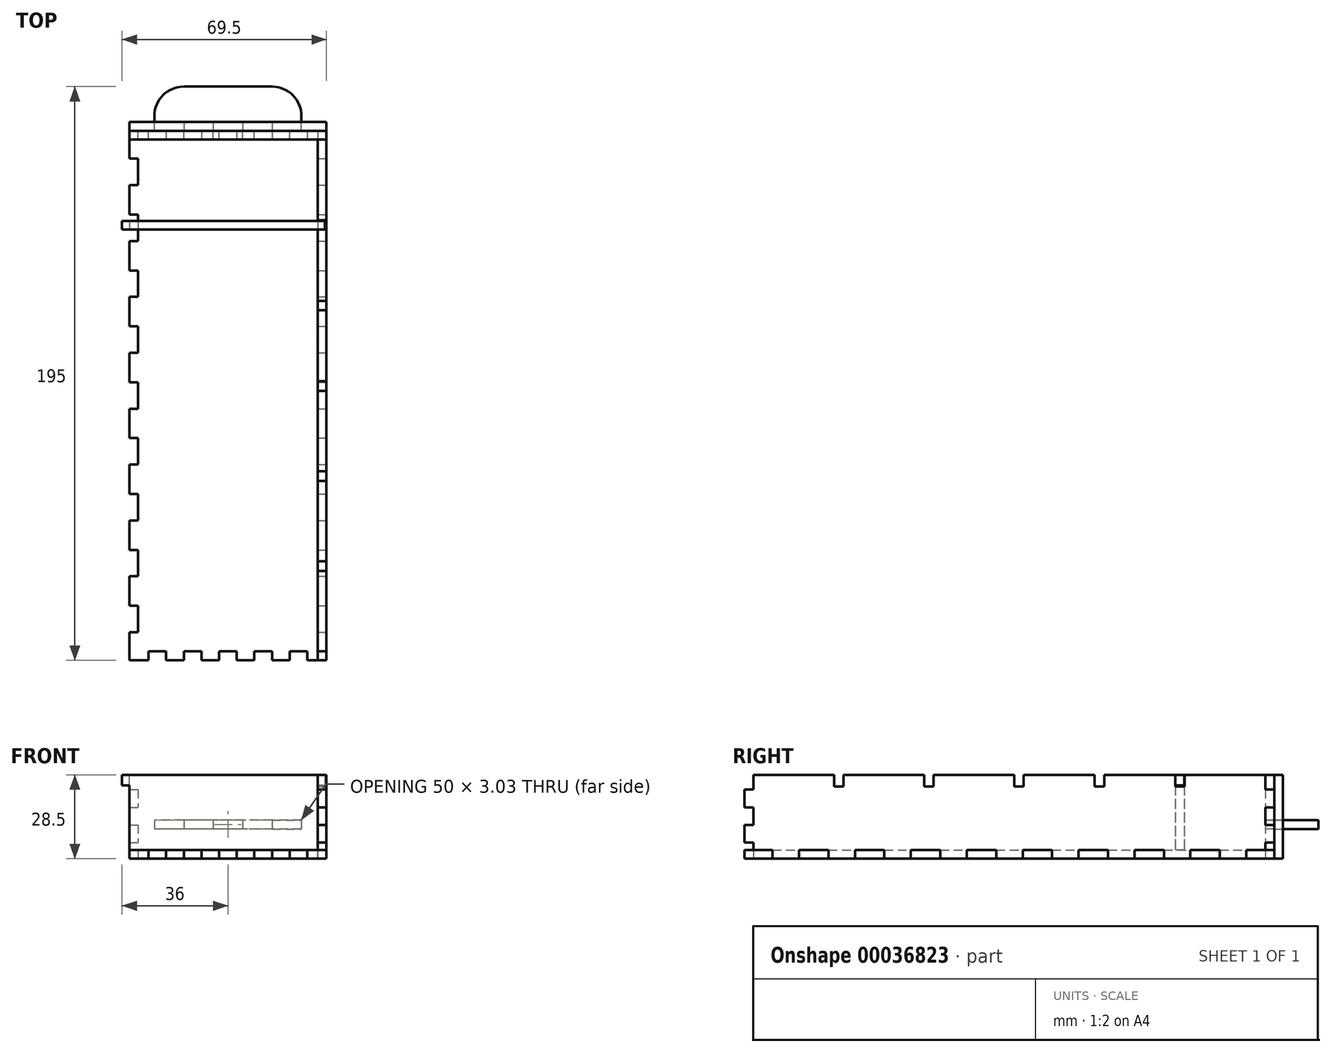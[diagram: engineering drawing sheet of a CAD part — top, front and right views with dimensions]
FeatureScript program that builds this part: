
annotation { "Feature Type Name" : "Feature", "Feature Type Description" : "" }
export const myFeature = defineFeature(function(context is Context, id is Id, definition is map)
    precondition{}
    {
        {
            var Q0;
            Q0=qCreatedBy(makeId("Front.planeOp"),FACE);
            var sketch = newSketch(context, id + "F0", { "sketchPlane" : qUnion([Q0])});
            skLineSegment(sketch, "E0.bottom", {"start": v(0, 0) * mm, "end": v(67, 0) * mm});
            skLineSegment(sketch, "E0.top", {"start": v(0, 28.5) * mm, "end": v(67, 28.5) * mm});
            skLineSegment(sketch, "E0.left", {"start": v(0, 0) * mm, "end": v(0, 28.5) * mm});
            skLineSegment(sketch, "E0.right", {"start": v(67, 0) * mm, "end": v(67, 28.5) * mm});
            skLineSegment(sketch, "E1.bottom", {"start": v(6.5, 0) * mm, "end": v(12.5, 0) * mm});
            skLineSegment(sketch, "E1.top", {"start": v(6.5, 3) * mm, "end": v(12.5, 3) * mm, "construction": true});
            skLineSegment(sketch, "E1.left", {"start": v(6.5, 0) * mm, "end": v(6.5, 3) * mm});
            skLineSegment(sketch, "E1.right", {"start": v(12.5, 0) * mm, "end": v(12.5, 3) * mm});
            skLineSegment(sketch, "E2.bottom", {"start": v(18.5, 0) * mm, "end": v(24.5, 0) * mm});
            skLineSegment(sketch, "E2.top", {"start": v(18.5, 3) * mm, "end": v(24.5, 3) * mm, "construction": true});
            skLineSegment(sketch, "E2.left", {"start": v(18.5, 0) * mm, "end": v(18.5, 3) * mm});
            skLineSegment(sketch, "E2.right", {"start": v(24.5, 0) * mm, "end": v(24.5, 3) * mm});
            skLineSegment(sketch, "E3.bottom", {"start": v(30.5, 0) * mm, "end": v(36.5, 0) * mm});
            skLineSegment(sketch, "E3.top", {"start": v(30.5, 3) * mm, "end": v(36.5, 3) * mm, "construction": true});
            skLineSegment(sketch, "E3.left", {"start": v(30.5, 0) * mm, "end": v(30.5, 3) * mm});
            skLineSegment(sketch, "E3.right", {"start": v(36.5, 0) * mm, "end": v(36.5, 3) * mm});
            skLineSegment(sketch, "E4.bottom", {"start": v(42.5, 0) * mm, "end": v(48.5, 0) * mm});
            skLineSegment(sketch, "E4.top", {"start": v(42.5, 3) * mm, "end": v(48.5, 3) * mm, "construction": true});
            skLineSegment(sketch, "E4.left", {"start": v(42.5, 0) * mm, "end": v(42.5, 3) * mm});
            skLineSegment(sketch, "E4.right", {"start": v(48.5, 0) * mm, "end": v(48.5, 3) * mm});
            skLineSegment(sketch, "E5.bottom", {"start": v(54.5, 0) * mm, "end": v(60.5, 0) * mm});
            skLineSegment(sketch, "E5.top", {"start": v(54.5, 3) * mm, "end": v(60.5, 3) * mm, "construction": true});
            skLineSegment(sketch, "E5.left", {"start": v(54.5, 0) * mm, "end": v(54.5, 3) * mm});
            skLineSegment(sketch, "E5.right", {"start": v(60.5, 0) * mm, "end": v(60.5, 3) * mm});
            skLineSegment(sketch, "E6.bottom", {"start": v(0, 23.5) * mm, "end": v(3, 23.5) * mm});
            skLineSegment(sketch, "E6.top", {"start": v(0, 17.5) * mm, "end": v(3, 17.5) * mm});
            skLineSegment(sketch, "E6.left", {"start": v(0, 23.5) * mm, "end": v(0, 17.5) * mm});
            skLineSegment(sketch, "E6.right", {"start": v(3, 23.5) * mm, "end": v(3, 17.5) * mm});
            skLineSegment(sketch, "E7.bottom", {"start": v(0, 11.5) * mm, "end": v(3, 11.5) * mm});
            skLineSegment(sketch, "E7.top", {"start": v(0, 5.5) * mm, "end": v(3, 5.5) * mm});
            skLineSegment(sketch, "E7.left", {"start": v(0, 11.5) * mm, "end": v(0, 5.5) * mm});
            skLineSegment(sketch, "E7.right", {"start": v(3, 11.5) * mm, "end": v(3, 5.5) * mm});
            skLineSegment(sketch, "E8.bottom", {"start": v(67, 23.5) * mm, "end": v(64, 23.5) * mm});
            skLineSegment(sketch, "E8.top", {"start": v(67, 17.5) * mm, "end": v(64, 17.5) * mm});
            skLineSegment(sketch, "E8.left", {"start": v(67, 23.5) * mm, "end": v(67, 17.5) * mm});
            skLineSegment(sketch, "E8.right", {"start": v(64, 23.5) * mm, "end": v(64, 17.5) * mm});
            skLineSegment(sketch, "E9.bottom", {"start": v(67, 11.5) * mm, "end": v(64, 11.5) * mm});
            skLineSegment(sketch, "E9.top", {"start": v(67, 5.5) * mm, "end": v(64, 5.5) * mm});
            skLineSegment(sketch, "E9.left", {"start": v(67, 11.5) * mm, "end": v(67, 5.5) * mm});
            skLineSegment(sketch, "E9.right", {"start": v(64, 11.5) * mm, "end": v(64, 5.5) * mm});
            skLineSegment(sketch, "E10", {"start": v(3, 17.5) * mm, "end": v(3, 11.5) * mm});
            skLineSegment(sketch, "E11", {"start": v(12.5, 3) * mm, "end": v(18.5, 3) * mm});
            skLineSegment(sketch, "E12", {"start": v(24.5, 3) * mm, "end": v(30.5, 3) * mm});
            skLineSegment(sketch, "E13", {"start": v(36.5, 3) * mm, "end": v(42.5, 3) * mm});
            skLineSegment(sketch, "E14", {"start": v(48.5, 3) * mm, "end": v(54.5, 3) * mm});
            skLineSegment(sketch, "E15", {"start": v(64, 11.5) * mm, "end": v(64, 17.5) * mm});
            skLineSegment(sketch, "E16", {"start": v(6.5, 3) * mm, "end": v(0, 3) * mm});
            skLineSegment(sketch, "E17", {"start": v(60.5, 3) * mm, "end": v(67, 3) * mm});
            skLineSegment(sketch, "E18.bottom", {"start": v(48.5, 13.14) * mm, "end": v(38.5, 13.14) * mm});
            skLineSegment(sketch, "E18.top", {"start": v(48.5, 10.1) * mm, "end": v(38.5, 10.1) * mm});
            skLineSegment(sketch, "E18.left", {"start": v(48.5, 13.14) * mm, "end": v(48.5, 10.1) * mm});
            skLineSegment(sketch, "E18.right", {"start": v(38.5, 13.14) * mm, "end": v(38.5, 10.1) * mm});
            skLineSegment(sketch, "E19.bottom", {"start": v(28.5, 13.14) * mm, "end": v(18.5, 13.14) * mm});
            skLineSegment(sketch, "E19.top", {"start": v(28.5, 10.1) * mm, "end": v(18.5, 10.1) * mm});
            skLineSegment(sketch, "E19.left", {"start": v(28.5, 13.14) * mm, "end": v(28.5, 10.1) * mm});
            skLineSegment(sketch, "E19.right", {"start": v(18.5, 13.14) * mm, "end": v(18.5, 10.1) * mm});
            skLineSegment(sketch, "E20.bottom", {"start": v(48.5, 10.1) * mm, "end": v(64, 10.1) * mm, "construction": true});
            skLineSegment(sketch, "E20.top", {"start": v(48.5, 10.1) * mm, "end": v(64, 10.1) * mm, "construction": true});
            skLineSegment(sketch, "E20.left", {"start": v(48.5, 10.1) * mm, "end": v(48.5, 10.1) * mm});
            skLineSegment(sketch, "E20.right", {"start": v(64, 10.1) * mm, "end": v(64, 10.1) * mm});
            skLineSegment(sketch, "E21.bottom", {"start": v(18.5, 10.1) * mm, "end": v(3, 10.1) * mm, "construction": true});
            skLineSegment(sketch, "E21.top", {"start": v(18.5, 10.1) * mm, "end": v(3, 10.1) * mm, "construction": true});
            skLineSegment(sketch, "E21.left", {"start": v(18.5, 10.1) * mm, "end": v(18.5, 10.1) * mm});
            skLineSegment(sketch, "E21.right", {"start": v(3, 10.1) * mm, "end": v(3, 10.1) * mm});
            skSolve(sketch);
        }
        {
            var Q0;
            {var subQ3=sQuery(id+"F0.wireOp",EDGE,"E0.top");Q0=makeQuery(id+"F0.imprint","IMPRINT",FACE,{"disambiguationData":[TD([[makeQuery(id+"F0.imprint","IMPRINT",EDGE,{"derivedFrom":subQ3}),-1.0]])]});}
            var Q1;
            {var subQ1=sQuery(id+"F0.wireOp",EDGE,"E6.top");Q1=makeQuery(id+"F0.imprint","IMPRINT",FACE,{"disambiguationData":[TD([[makeQuery(id+"F0.imprint","IMPRINT",EDGE,{"derivedFrom":subQ1}),-1.0]])]});}
            var Q2;
            {var subQ1=sQuery(id+"F0.wireOp",EDGE,"E8.top");Q2=makeQuery(id+"F0.imprint","IMPRINT",FACE,{"disambiguationData":[TD([[makeQuery(id+"F0.imprint","IMPRINT",EDGE,{"derivedFrom":subQ1}),1.0]])]});}
            extrude(context, id + "F1", {"entities" : qUnion([Q0, Q1, Q2]), "depth" : 3 * mm});
        }
        {
            var Q0;
            Q0=qCreatedBy(makeId("Top.planeOp"),FACE);
            var sketch = newSketch(context, id + "F2", { "sketchPlane" : qUnion([Q0])});
            skLineSegment(sketch, "E22.top", {"start": v(0, -180) * mm, "end": v(67, -180) * mm});
            skLineSegment(sketch, "E22.left", {"start": v(0, 0) * mm, "end": v(0, -180) * mm});
            skLineSegment(sketch, "E22.right", {"start": v(67, 0) * mm, "end": v(67, -180) * mm});
            skLineSegment(sketch, "E23.bottom", {"start": v(6.5, -180) * mm, "end": v(12.5, -180) * mm});
            skLineSegment(sketch, "E23.top", {"start": v(6.5, -177) * mm, "end": v(12.5, -177) * mm});
            skLineSegment(sketch, "E23.left", {"start": v(6.5, -180) * mm, "end": v(6.5, -177) * mm});
            skLineSegment(sketch, "E23.right", {"start": v(12.5, -180) * mm, "end": v(12.5, -177) * mm});
            skLineSegment(sketch, "E24.bottom", {"start": v(18.5, -180) * mm, "end": v(24.5, -180) * mm});
            skLineSegment(sketch, "E24.top", {"start": v(18.5, -177) * mm, "end": v(24.5, -177) * mm});
            skLineSegment(sketch, "E24.left", {"start": v(18.5, -180) * mm, "end": v(18.5, -177) * mm});
            skLineSegment(sketch, "E24.right", {"start": v(24.5, -180) * mm, "end": v(24.5, -177) * mm});
            skLineSegment(sketch, "E25.bottom", {"start": v(30.5, -180) * mm, "end": v(36.5, -180) * mm});
            skLineSegment(sketch, "E25.top", {"start": v(30.5, -177) * mm, "end": v(36.5, -177) * mm});
            skLineSegment(sketch, "E25.left", {"start": v(30.5, -180) * mm, "end": v(30.5, -177) * mm});
            skLineSegment(sketch, "E25.right", {"start": v(36.5, -180) * mm, "end": v(36.5, -177) * mm});
            skLineSegment(sketch, "E26.bottom", {"start": v(42.5, -180) * mm, "end": v(48.5, -180) * mm});
            skLineSegment(sketch, "E26.top", {"start": v(42.5, -177) * mm, "end": v(48.5, -177) * mm});
            skLineSegment(sketch, "E26.left", {"start": v(42.5, -180) * mm, "end": v(42.5, -177) * mm});
            skLineSegment(sketch, "E26.right", {"start": v(48.5, -180) * mm, "end": v(48.5, -177) * mm});
            skLineSegment(sketch, "E27.bottom", {"start": v(54.5, -180) * mm, "end": v(60.5, -180) * mm});
            skLineSegment(sketch, "E27.top", {"start": v(54.5, -177) * mm, "end": v(60.5, -177) * mm});
            skLineSegment(sketch, "E27.left", {"start": v(54.5, -180) * mm, "end": v(54.5, -177) * mm});
            skLineSegment(sketch, "E27.right", {"start": v(60.5, -180) * mm, "end": v(60.5, -177) * mm});
            skLineSegment(sketch, "E28.top", {"start": v(0, -18.5) * mm, "end": v(3, -18.5) * mm});
            skLineSegment(sketch, "E28.left", {"start": v(0, -9.5) * mm, "end": v(0, -18.5) * mm});
            skLineSegment(sketch, "E28.right", {"start": v(3, -9.5) * mm, "end": v(3, -18.5) * mm});
            skLineSegment(sketch, "E29.bottom", {"start": v(0, -28.5) * mm, "end": v(3, -28.5) * mm});
            skLineSegment(sketch, "E29.top", {"start": v(0, -37.5) * mm, "end": v(3, -37.5) * mm});
            skLineSegment(sketch, "E29.left", {"start": v(0, -28.5) * mm, "end": v(0, -37.5) * mm});
            skLineSegment(sketch, "E29.right", {"start": v(3, -28.5) * mm, "end": v(3, -37.5) * mm});
            skLineSegment(sketch, "E30.bottom", {"start": v(0, -47.5) * mm, "end": v(3, -47.5) * mm});
            skLineSegment(sketch, "E30.top", {"start": v(0, -56.5) * mm, "end": v(3, -56.5) * mm});
            skLineSegment(sketch, "E30.left", {"start": v(0, -47.5) * mm, "end": v(0, -56.5) * mm});
            skLineSegment(sketch, "E30.right", {"start": v(3, -47.5) * mm, "end": v(3, -56.5) * mm});
            skLineSegment(sketch, "E31.bottom", {"start": v(0, -66.5) * mm, "end": v(3, -66.5) * mm});
            skLineSegment(sketch, "E31.top", {"start": v(0, -75.5) * mm, "end": v(3, -75.5) * mm});
            skLineSegment(sketch, "E31.left", {"start": v(0, -66.5) * mm, "end": v(0, -75.5) * mm});
            skLineSegment(sketch, "E31.right", {"start": v(3, -66.5) * mm, "end": v(3, -75.5) * mm});
            skLineSegment(sketch, "E32.bottom", {"start": v(0, -85.5) * mm, "end": v(3, -85.5) * mm});
            skLineSegment(sketch, "E32.top", {"start": v(0, -94.5) * mm, "end": v(3, -94.5) * mm});
            skLineSegment(sketch, "E32.left", {"start": v(0, -85.5) * mm, "end": v(0, -94.5) * mm});
            skLineSegment(sketch, "E32.right", {"start": v(3, -85.5) * mm, "end": v(3, -94.5) * mm});
            skLineSegment(sketch, "E33.bottom", {"start": v(0, -104.5) * mm, "end": v(3, -104.5) * mm});
            skLineSegment(sketch, "E33.top", {"start": v(0, -113.5) * mm, "end": v(3, -113.5) * mm});
            skLineSegment(sketch, "E33.left", {"start": v(0, -104.5) * mm, "end": v(0, -113.5) * mm});
            skLineSegment(sketch, "E33.right", {"start": v(3, -104.5) * mm, "end": v(3, -113.5) * mm});
            skLineSegment(sketch, "E34.bottom", {"start": v(0, -123.5) * mm, "end": v(3, -123.5) * mm});
            skLineSegment(sketch, "E34.top", {"start": v(0, -132.5) * mm, "end": v(3, -132.5) * mm});
            skLineSegment(sketch, "E34.left", {"start": v(0, -123.5) * mm, "end": v(0, -132.5) * mm});
            skLineSegment(sketch, "E34.right", {"start": v(3, -123.5) * mm, "end": v(3, -132.5) * mm});
            skLineSegment(sketch, "E35.bottom", {"start": v(0, -142.5) * mm, "end": v(3, -142.5) * mm});
            skLineSegment(sketch, "E35.top", {"start": v(0, -151.5) * mm, "end": v(3, -151.5) * mm});
            skLineSegment(sketch, "E35.left", {"start": v(0, -142.5) * mm, "end": v(0, -151.5) * mm});
            skLineSegment(sketch, "E35.right", {"start": v(3, -142.5) * mm, "end": v(3, -151.5) * mm});
            skLineSegment(sketch, "E36.bottom", {"start": v(0, -161.5) * mm, "end": v(3, -161.5) * mm});
            skLineSegment(sketch, "E36.top", {"start": v(0, -170.5) * mm, "end": v(3, -170.5) * mm});
            skLineSegment(sketch, "E36.left", {"start": v(0, -161.5) * mm, "end": v(0, -170.5) * mm});
            skLineSegment(sketch, "E36.right", {"start": v(3, -161.5) * mm, "end": v(3, -170.5) * mm});
            skLineSegment(sketch, "E37", {"start": v(3, -161.5) * mm, "end": v(3, -151.5) * mm, "construction": true});
            skLineSegment(sketch, "E38", {"start": v(3, -142.5) * mm, "end": v(3, -132.5) * mm, "construction": true});
            skLineSegment(sketch, "E39", {"start": v(3, -123.5) * mm, "end": v(3, -113.5) * mm, "construction": true});
            skLineSegment(sketch, "E40", {"start": v(3, -104.5) * mm, "end": v(3, -94.5) * mm, "construction": true});
            skLineSegment(sketch, "E41", {"start": v(3, -18.5) * mm, "end": v(3, -28.5) * mm, "construction": true});
            skLineSegment(sketch, "E42", {"start": v(3, -37.5) * mm, "end": v(3, -47.5) * mm, "construction": true});
            skLineSegment(sketch, "E43", {"start": v(3, -56.5) * mm, "end": v(3, -66.5) * mm, "construction": true});
            skLineSegment(sketch, "E44", {"start": v(3, -75.5) * mm, "end": v(3, -85.5) * mm, "construction": true});
            skLineSegment(sketch, "E45", {"start": v(3, -170.5) * mm, "end": v(3, -177) * mm, "construction": true});
            skLineSegment(sketch, "E46.bottom", {"start": v(67, -170.5) * mm, "end": v(64, -170.5) * mm});
            skLineSegment(sketch, "E46.top", {"start": v(67, -161.5) * mm, "end": v(64, -161.5) * mm});
            skLineSegment(sketch, "E46.left", {"start": v(67, -170.5) * mm, "end": v(67, -161.5) * mm});
            skLineSegment(sketch, "E46.right", {"start": v(64, -170.5) * mm, "end": v(64, -161.5) * mm});
            skLineSegment(sketch, "E47.bottom", {"start": v(67, -151.5) * mm, "end": v(64, -151.5) * mm});
            skLineSegment(sketch, "E47.top", {"start": v(67, -142.5) * mm, "end": v(64, -142.5) * mm});
            skLineSegment(sketch, "E47.left", {"start": v(67, -151.5) * mm, "end": v(67, -142.5) * mm});
            skLineSegment(sketch, "E47.right", {"start": v(64, -151.5) * mm, "end": v(64, -142.5) * mm});
            skPoint(sketch, "E48.oppositeSnap0", {"position": v(1.5, -123.5) * mm});
            skLineSegment(sketch, "E48.bottom", {"start": v(67, -132.5) * mm, "end": v(64, -132.5) * mm});
            skLineSegment(sketch, "E48.top", {"start": v(67, -123.5) * mm, "end": v(64, -123.5) * mm});
            skLineSegment(sketch, "E48.left", {"start": v(67, -132.5) * mm, "end": v(67, -123.5) * mm});
            skLineSegment(sketch, "E48.right", {"start": v(64, -132.5) * mm, "end": v(64, -123.5) * mm});
            skPoint(sketch, "E49.firstSnap0", {"position": v(1.5, -113.5) * mm});
            skLineSegment(sketch, "E49.bottom", {"start": v(67, -113.5) * mm, "end": v(64, -113.5) * mm});
            skLineSegment(sketch, "E49.top", {"start": v(67, -104.5) * mm, "end": v(64, -104.5) * mm});
            skLineSegment(sketch, "E49.left", {"start": v(67, -113.5) * mm, "end": v(67, -104.5) * mm});
            skLineSegment(sketch, "E49.right", {"start": v(64, -113.5) * mm, "end": v(64, -104.5) * mm});
            skLineSegment(sketch, "E50.bottom", {"start": v(67, -94.5) * mm, "end": v(64, -94.5) * mm});
            skLineSegment(sketch, "E50.top", {"start": v(67, -85.5) * mm, "end": v(64, -85.5) * mm});
            skLineSegment(sketch, "E50.left", {"start": v(67, -94.5) * mm, "end": v(67, -85.5) * mm});
            skLineSegment(sketch, "E50.right", {"start": v(64, -94.5) * mm, "end": v(64, -85.5) * mm});
            skLineSegment(sketch, "E51.bottom", {"start": v(67, -75.5) * mm, "end": v(64, -75.5) * mm});
            skLineSegment(sketch, "E51.top", {"start": v(67, -66.5) * mm, "end": v(64, -66.5) * mm});
            skLineSegment(sketch, "E51.left", {"start": v(67, -75.5) * mm, "end": v(67, -66.5) * mm});
            skLineSegment(sketch, "E51.right", {"start": v(64, -75.5) * mm, "end": v(64, -66.5) * mm});
            skLineSegment(sketch, "E52.bottom", {"start": v(67, -56.5) * mm, "end": v(64, -56.5) * mm});
            skLineSegment(sketch, "E52.top", {"start": v(67, -47.5) * mm, "end": v(64, -47.5) * mm});
            skLineSegment(sketch, "E52.left", {"start": v(67, -56.5) * mm, "end": v(67, -47.5) * mm});
            skLineSegment(sketch, "E52.right", {"start": v(64, -56.5) * mm, "end": v(64, -47.5) * mm});
            skLineSegment(sketch, "E53.bottom", {"start": v(67, -37.5) * mm, "end": v(64, -37.5) * mm});
            skLineSegment(sketch, "E53.top", {"start": v(67, -28.5) * mm, "end": v(64, -28.5) * mm});
            skLineSegment(sketch, "E53.left", {"start": v(67, -37.5) * mm, "end": v(67, -28.5) * mm});
            skLineSegment(sketch, "E53.right", {"start": v(64, -37.5) * mm, "end": v(64, -28.5) * mm});
            skLineSegment(sketch, "E54.bottom", {"start": v(67, -18.5) * mm, "end": v(64, -18.5) * mm});
            skLineSegment(sketch, "E54.left", {"start": v(67, -18.5) * mm, "end": v(67, -9.5) * mm});
            skLineSegment(sketch, "E54.right", {"start": v(64, -18.5) * mm, "end": v(64, -9.5) * mm});
            skLineSegment(sketch, "E55.0.0", {"start": v(54.5, 0) * mm, "end": v(60.5, 0) * mm});
            skLineSegment(sketch, "E55.0.1", {"start": v(60.5, 0) * mm, "end": v(60.5, -3) * mm});
            skLineSegment(sketch, "E55.0.2", {"start": v(60.5, -3) * mm, "end": v(54.5, -3) * mm});
            skLineSegment(sketch, "E55.0.3", {"start": v(54.5, -3) * mm, "end": v(54.5, 0) * mm});
            skLineSegment(sketch, "E56.0.0", {"start": v(42.5, 0) * mm, "end": v(48.5, 0) * mm});
            skLineSegment(sketch, "E56.0.1", {"start": v(48.5, 0) * mm, "end": v(48.5, -3) * mm});
            skLineSegment(sketch, "E56.0.2", {"start": v(48.5, -3) * mm, "end": v(42.5, -3) * mm});
            skLineSegment(sketch, "E56.0.3", {"start": v(42.5, -3) * mm, "end": v(42.5, 0) * mm});
            skLineSegment(sketch, "E57.0.0", {"start": v(30.5, 0) * mm, "end": v(36.5, 0) * mm});
            skLineSegment(sketch, "E57.0.1", {"start": v(36.5, 0) * mm, "end": v(36.5, -3) * mm});
            skLineSegment(sketch, "E57.0.2", {"start": v(36.5, -3) * mm, "end": v(30.5, -3) * mm});
            skLineSegment(sketch, "E57.0.3", {"start": v(30.5, -3) * mm, "end": v(30.5, 0) * mm});
            skLineSegment(sketch, "E58.0.0", {"start": v(18.5, 0) * mm, "end": v(24.5, 0) * mm});
            skLineSegment(sketch, "E58.0.1", {"start": v(24.5, 0) * mm, "end": v(24.5, -3) * mm});
            skLineSegment(sketch, "E58.0.2", {"start": v(24.5, -3) * mm, "end": v(18.5, -3) * mm});
            skLineSegment(sketch, "E58.0.3", {"start": v(18.5, -3) * mm, "end": v(18.5, 0) * mm});
            skLineSegment(sketch, "E59.0.0", {"start": v(6.5, 0) * mm, "end": v(12.5, 0) * mm});
            skLineSegment(sketch, "E59.0.1", {"start": v(12.5, 0) * mm, "end": v(12.5, -3) * mm});
            skLineSegment(sketch, "E59.0.2", {"start": v(12.5, -3) * mm, "end": v(6.5, -3) * mm});
            skLineSegment(sketch, "E59.0.3", {"start": v(6.5, -3) * mm, "end": v(6.5, 0) * mm});
            skLineSegment(sketch, "E60", {"start": v(67, -9.5) * mm, "end": v(64, -9.5) * mm});
            skLineSegment(sketch, "E61", {"start": v(3, -9.5) * mm, "end": v(0, -9.5) * mm});
            skLineSegment(sketch, "E62", {"start": v(0, 0) * mm, "end": v(67, 0) * mm});
            skSolve(sketch);
        }
        {
            var Q0;
            Q0=makeQuery(id+"F2.imprint","IMPRINT",FACE,{"disambiguationData":[TD([[makeQuery(id+"F2.imprint","IMPRINT",EDGE,{"derivedFrom":sQuery(id+"F2.wireOp",EDGE,"E23.top")}),1.0]])]});
            extrude(context, id + "F3", {"entities" : qUnion([Q0]), "depth" : 3 * mm});
        }
        {
            var Q0;
            {var subQ0=sQuery(id+"F2.wireOp",EDGE,"E22.right");Q0=makeQuery(id+"F3.opExtrude","SWEPT_FACE",FACE,{"disambiguationData":[OSD([subQ0]),TDD([makeQuery(id+"F2.imprint","IMPRINT",EDGE,{"disambiguationData":[TD([[makeQuery(id+"F2.imprint","INTERSECT",VERTEX,{"derivedFrom":[subQ0,sQuery(id+"F2.wireOp",EDGE,"E53.top"),sQuery(id+"F2.wireOp",EDGE,"E53.left")]}),1.0]])],"derivedFrom":subQ0})])]});}
            var sketch = newSketch(context, id + "F4", { "sketchPlane" : qUnion([Q0])});
            skLineSegment(sketch, "E63.0.0", {"start": v(-18.5, 0) * mm, "end": v(-9.5, 0) * mm});
            skLineSegment(sketch, "E63.0.1", {"start": v(-9.5, 0) * mm, "end": v(-9.5, 3) * mm});
            skLineSegment(sketch, "E63.0.2", {"start": v(-9.5, 3) * mm, "end": v(-18.5, 3) * mm});
            skLineSegment(sketch, "E63.0.3", {"start": v(-18.5, 3) * mm, "end": v(-18.5, 0) * mm});
            skLineSegment(sketch, "E64.0.0", {"start": v(-37.5, 0) * mm, "end": v(-28.5, 0) * mm});
            skLineSegment(sketch, "E64.0.1", {"start": v(-28.5, 0) * mm, "end": v(-28.5, 3) * mm});
            skLineSegment(sketch, "E64.0.2", {"start": v(-28.5, 3) * mm, "end": v(-37.5, 3) * mm});
            skLineSegment(sketch, "E64.0.3", {"start": v(-37.5, 3) * mm, "end": v(-37.5, 0) * mm});
            skLineSegment(sketch, "E65.0.0", {"start": v(0, 5.5) * mm, "end": v(0, 11.5) * mm});
            skLineSegment(sketch, "E65.0.1", {"start": v(0, 11.5) * mm, "end": v(-3, 11.5) * mm});
            skLineSegment(sketch, "E65.0.2", {"start": v(-3, 11.5) * mm, "end": v(-3, 5.5) * mm});
            skLineSegment(sketch, "E65.0.3", {"start": v(-3, 5.5) * mm, "end": v(0, 5.5) * mm});
            skLineSegment(sketch, "E66.0.0", {"start": v(0, 17.5) * mm, "end": v(0, 23.5) * mm});
            skLineSegment(sketch, "E66.0.1", {"start": v(0, 23.5) * mm, "end": v(-3, 23.5) * mm});
            skLineSegment(sketch, "E66.0.2", {"start": v(-3, 23.5) * mm, "end": v(-3, 17.5) * mm});
            skLineSegment(sketch, "E66.0.3", {"start": v(-3, 17.5) * mm, "end": v(0, 17.5) * mm});
            skLineSegment(sketch, "E67.0.0", {"start": v(-56.5, 0) * mm, "end": v(-47.5, 0) * mm});
            skLineSegment(sketch, "E67.0.1", {"start": v(-47.5, 0) * mm, "end": v(-47.5, 3) * mm});
            skLineSegment(sketch, "E67.0.2", {"start": v(-47.5, 3) * mm, "end": v(-56.5, 3) * mm});
            skLineSegment(sketch, "E67.0.3", {"start": v(-56.5, 3) * mm, "end": v(-56.5, 0) * mm});
            skLineSegment(sketch, "E68.0.0", {"start": v(-75.5, 0) * mm, "end": v(-66.5, 0) * mm});
            skLineSegment(sketch, "E68.0.1", {"start": v(-66.5, 0) * mm, "end": v(-66.5, 3) * mm});
            skLineSegment(sketch, "E68.0.2", {"start": v(-66.5, 3) * mm, "end": v(-75.5, 3) * mm});
            skLineSegment(sketch, "E68.0.3", {"start": v(-75.5, 3) * mm, "end": v(-75.5, 0) * mm});
            skLineSegment(sketch, "E69.0.0", {"start": v(-94.5, 0) * mm, "end": v(-85.5, 0) * mm});
            skLineSegment(sketch, "E69.0.1", {"start": v(-85.5, 0) * mm, "end": v(-85.5, 3) * mm});
            skLineSegment(sketch, "E69.0.2", {"start": v(-85.5, 3) * mm, "end": v(-94.5, 3) * mm});
            skLineSegment(sketch, "E69.0.3", {"start": v(-94.5, 3) * mm, "end": v(-94.5, 0) * mm});
            skLineSegment(sketch, "E70.0.0", {"start": v(-113.5, 0) * mm, "end": v(-104.5, 0) * mm});
            skLineSegment(sketch, "E70.0.1", {"start": v(-104.5, 0) * mm, "end": v(-104.5, 3) * mm});
            skLineSegment(sketch, "E70.0.2", {"start": v(-104.5, 3) * mm, "end": v(-113.5, 3) * mm});
            skLineSegment(sketch, "E70.0.3", {"start": v(-113.5, 3) * mm, "end": v(-113.5, 0) * mm});
            skLineSegment(sketch, "E71.0.0", {"start": v(-132.5, 0) * mm, "end": v(-123.5, 0) * mm});
            skLineSegment(sketch, "E71.0.1", {"start": v(-123.5, 0) * mm, "end": v(-123.5, 3) * mm});
            skLineSegment(sketch, "E71.0.2", {"start": v(-123.5, 3) * mm, "end": v(-132.5, 3) * mm});
            skLineSegment(sketch, "E71.0.3", {"start": v(-132.5, 3) * mm, "end": v(-132.5, 0) * mm});
            skLineSegment(sketch, "E72.0.0", {"start": v(-170.5, 0) * mm, "end": v(-161.5, 0) * mm});
            skLineSegment(sketch, "E72.0.1", {"start": v(-161.5, 0) * mm, "end": v(-161.5, 3) * mm});
            skLineSegment(sketch, "E72.0.2", {"start": v(-161.5, 3) * mm, "end": v(-170.5, 3) * mm});
            skLineSegment(sketch, "E72.0.3", {"start": v(-170.5, 3) * mm, "end": v(-170.5, 0) * mm});
            skLineSegment(sketch, "E73.0.0", {"start": v(-151.5, 0) * mm, "end": v(-142.5, 0) * mm});
            skLineSegment(sketch, "E73.0.1", {"start": v(-142.5, 0) * mm, "end": v(-142.5, 3) * mm});
            skLineSegment(sketch, "E73.0.2", {"start": v(-142.5, 3) * mm, "end": v(-151.5, 3) * mm});
            skLineSegment(sketch, "E73.0.3", {"start": v(-151.5, 3) * mm, "end": v(-151.5, 0) * mm});
            skLineSegment(sketch, "E74.bottom", {"start": v(-180, 23.5) * mm, "end": v(-177, 23.5) * mm});
            skLineSegment(sketch, "E74.top", {"start": v(-180, 17.5) * mm, "end": v(-177, 17.5) * mm});
            skLineSegment(sketch, "E74.left", {"start": v(-180, 23.5) * mm, "end": v(-180, 17.5) * mm});
            skLineSegment(sketch, "E74.right", {"start": v(-177, 23.5) * mm, "end": v(-177, 17.5) * mm});
            skLineSegment(sketch, "E75.bottom", {"start": v(-180, 11.5) * mm, "end": v(-177, 11.5) * mm});
            skLineSegment(sketch, "E75.top", {"start": v(-180, 5.5) * mm, "end": v(-177, 5.5) * mm});
            skLineSegment(sketch, "E75.left", {"start": v(-180, 11.5) * mm, "end": v(-180, 5.5) * mm});
            skLineSegment(sketch, "E75.right", {"start": v(-177, 11.5) * mm, "end": v(-177, 5.5) * mm});
            skLineSegment(sketch, "E76.bottom", {"start": v(0, 0.09) * mm, "end": v(-180, 0.09) * mm});
            skLineSegment(sketch, "E76.top", {"start": v(0, 28.5) * mm, "end": v(-180, 28.5) * mm});
            skLineSegment(sketch, "E76.left", {"start": v(0, 0.09) * mm, "end": v(0, 28.5) * mm});
            skLineSegment(sketch, "E76.right", {"start": v(-180, 0.09) * mm, "end": v(-180, 28.5) * mm});
            skLineSegment(sketch, "E77.0.0", {"start": v(-85.5, 0) * mm, "end": v(-75.5, 0) * mm});
            skLineSegment(sketch, "E77.0.1", {"start": v(-75.5, 0) * mm, "end": v(-75.5, 3) * mm});
            skLineSegment(sketch, "E77.0.2", {"start": v(-75.5, 3) * mm, "end": v(-85.5, 3) * mm});
            skLineSegment(sketch, "E77.0.3", {"start": v(-85.5, 3) * mm, "end": v(-85.5, 0) * mm});
            skLineSegment(sketch, "E78.0.0", {"start": v(-66.5, 0) * mm, "end": v(-56.5, 0) * mm});
            skLineSegment(sketch, "E78.0.1", {"start": v(-56.5, 0) * mm, "end": v(-56.5, 3) * mm});
            skLineSegment(sketch, "E78.0.2", {"start": v(-56.5, 3) * mm, "end": v(-66.5, 3) * mm});
            skLineSegment(sketch, "E78.0.3", {"start": v(-66.5, 3) * mm, "end": v(-66.5, 0) * mm});
            skLineSegment(sketch, "E79.0.0", {"start": v(-47.5, 0) * mm, "end": v(-37.5, 0) * mm});
            skLineSegment(sketch, "E79.0.1", {"start": v(-37.5, 0) * mm, "end": v(-37.5, 3) * mm});
            skLineSegment(sketch, "E79.0.2", {"start": v(-37.5, 3) * mm, "end": v(-47.5, 3) * mm});
            skLineSegment(sketch, "E79.0.3", {"start": v(-47.5, 3) * mm, "end": v(-47.5, 0) * mm});
            skLineSegment(sketch, "E80.0.0", {"start": v(-28.5, 0) * mm, "end": v(-18.5, 0) * mm});
            skLineSegment(sketch, "E80.0.1", {"start": v(-18.5, 0) * mm, "end": v(-18.5, 3) * mm});
            skLineSegment(sketch, "E80.0.2", {"start": v(-18.5, 3) * mm, "end": v(-28.5, 3) * mm});
            skLineSegment(sketch, "E80.0.3", {"start": v(-28.5, 3) * mm, "end": v(-28.5, 0) * mm});
            skLineSegment(sketch, "E81.0.0", {"start": v(-9.5, 0) * mm, "end": v(0, 0) * mm});
            skLineSegment(sketch, "E81.0.1", {"start": v(0, 0) * mm, "end": v(0, 3) * mm});
            skLineSegment(sketch, "E81.0.2", {"start": v(0, 3) * mm, "end": v(-9.5, 3) * mm});
            skLineSegment(sketch, "E81.0.3", {"start": v(-9.5, 3) * mm, "end": v(-9.5, 0) * mm});
            skLineSegment(sketch, "E82.0.0", {"start": v(0, 11.5) * mm, "end": v(0, 17.5) * mm});
            skLineSegment(sketch, "E82.0.1", {"start": v(0, 17.5) * mm, "end": v(-3, 17.5) * mm});
            skLineSegment(sketch, "E82.0.2", {"start": v(-3, 17.5) * mm, "end": v(-3, 11.5) * mm});
            skLineSegment(sketch, "E82.0.3", {"start": v(-3, 11.5) * mm, "end": v(0, 11.5) * mm});
            skLineSegment(sketch, "E83.0.0", {"start": v(0, 23.5) * mm, "end": v(0, 28.5) * mm});
            skLineSegment(sketch, "E83.0.1", {"start": v(0, 28.5) * mm, "end": v(-3, 28.5) * mm});
            skLineSegment(sketch, "E83.0.2", {"start": v(-3, 28.5) * mm, "end": v(-3, 23.5) * mm});
            skLineSegment(sketch, "E83.0.3", {"start": v(-3, 23.5) * mm, "end": v(0, 23.5) * mm});
            skLineSegment(sketch, "E84.0.0", {"start": v(0, 3) * mm, "end": v(0, 5.5) * mm});
            skLineSegment(sketch, "E84.0.1", {"start": v(0, 5.5) * mm, "end": v(-3, 5.5) * mm});
            skLineSegment(sketch, "E84.0.2", {"start": v(-3, 5.5) * mm, "end": v(-3, 3) * mm});
            skLineSegment(sketch, "E84.0.3", {"start": v(-3, 3) * mm, "end": v(0, 3) * mm});
            skLineSegment(sketch, "E85.0.0", {"start": v(-104.5, 0) * mm, "end": v(-94.5, 0) * mm});
            skLineSegment(sketch, "E85.0.1", {"start": v(-94.5, 0) * mm, "end": v(-94.5, 3) * mm});
            skLineSegment(sketch, "E85.0.2", {"start": v(-94.5, 3) * mm, "end": v(-104.5, 3) * mm});
            skLineSegment(sketch, "E85.0.3", {"start": v(-104.5, 3) * mm, "end": v(-104.5, 0) * mm});
            skLineSegment(sketch, "E86.0.0", {"start": v(-123.5, 0) * mm, "end": v(-113.5, 0) * mm});
            skLineSegment(sketch, "E86.0.1", {"start": v(-113.5, 0) * mm, "end": v(-113.5, 3) * mm});
            skLineSegment(sketch, "E86.0.2", {"start": v(-113.5, 3) * mm, "end": v(-123.5, 3) * mm});
            skLineSegment(sketch, "E86.0.3", {"start": v(-123.5, 3) * mm, "end": v(-123.5, 0) * mm});
            skLineSegment(sketch, "E87.0.0", {"start": v(-142.5, 0) * mm, "end": v(-132.5, 0) * mm});
            skLineSegment(sketch, "E87.0.1", {"start": v(-132.5, 0) * mm, "end": v(-132.5, 3) * mm});
            skLineSegment(sketch, "E87.0.2", {"start": v(-132.5, 3) * mm, "end": v(-142.5, 3) * mm});
            skLineSegment(sketch, "E87.0.3", {"start": v(-142.5, 3) * mm, "end": v(-142.5, 0) * mm});
            skLineSegment(sketch, "E88.0.0", {"start": v(-161.5, 0) * mm, "end": v(-151.5, 0) * mm});
            skLineSegment(sketch, "E88.0.1", {"start": v(-151.5, 0) * mm, "end": v(-151.5, 3) * mm});
            skLineSegment(sketch, "E88.0.2", {"start": v(-151.5, 3) * mm, "end": v(-161.5, 3) * mm});
            skLineSegment(sketch, "E88.0.3", {"start": v(-161.5, 3) * mm, "end": v(-161.5, 0) * mm});
            skLineSegment(sketch, "E89.0.0", {"start": v(-180, 0) * mm, "end": v(-170.5, 0) * mm});
            skLineSegment(sketch, "E89.0.1", {"start": v(-170.5, 0) * mm, "end": v(-170.5, 3) * mm});
            skLineSegment(sketch, "E89.0.2", {"start": v(-170.5, 3) * mm, "end": v(-180, 3) * mm});
            skLineSegment(sketch, "E89.0.3", {"start": v(-180, 3) * mm, "end": v(-180, 0) * mm});
            skLineSegment(sketch, "E90", {"start": v(-177, 5.5) * mm, "end": v(-177, 3) * mm});
            skLineSegment(sketch, "E91", {"start": v(-177, 23.5) * mm, "end": v(-177, 28.5) * mm});
            skLineSegment(sketch, "E92", {"start": v(-177, 17.5) * mm, "end": v(-177, 11.5) * mm});
            skSolve(sketch);
        }
        {
            var Q0;
            Q0=makeQuery(id+"F4.imprint","IMPRINT",FACE,{"disambiguationData":[TD([[makeQuery(id+"F4.imprint","IMPRINT",EDGE,{"derivedFrom":sQuery(id+"F4.wireOp",EDGE,"E63.0.2")}),-1.0]])]});
            var Q1;
            {var subQ3=sQuery(id+"F4.wireOp",EDGE,"E72.0.2");Q1=makeQuery(id+"F4.imprint","IMPRINT",FACE,{"disambiguationData":[TD([[makeQuery(id+"F4.imprint","IMPRINT",EDGE,{"derivedFrom":subQ3}),1.0]])]});}
            var Q2;
            {var subQ3=sQuery(id+"F4.wireOp",EDGE,"E73.0.2");Q2=makeQuery(id+"F4.imprint","IMPRINT",FACE,{"disambiguationData":[TD([[makeQuery(id+"F4.imprint","IMPRINT",EDGE,{"derivedFrom":subQ3}),1.0]])]});}
            var Q3;
            {var subQ3=sQuery(id+"F4.wireOp",EDGE,"E71.0.2");Q3=makeQuery(id+"F4.imprint","IMPRINT",FACE,{"disambiguationData":[TD([[makeQuery(id+"F4.imprint","IMPRINT",EDGE,{"derivedFrom":subQ3}),1.0]])]});}
            var Q4;
            {var subQ3=sQuery(id+"F4.wireOp",EDGE,"E70.0.2");Q4=makeQuery(id+"F4.imprint","IMPRINT",FACE,{"disambiguationData":[TD([[makeQuery(id+"F4.imprint","IMPRINT",EDGE,{"derivedFrom":subQ3}),1.0]])]});}
            var Q5;
            {var subQ3=sQuery(id+"F4.wireOp",EDGE,"E69.0.2");Q5=makeQuery(id+"F4.imprint","IMPRINT",FACE,{"disambiguationData":[TD([[makeQuery(id+"F4.imprint","IMPRINT",EDGE,{"derivedFrom":subQ3}),1.0]])]});}
            var Q6;
            {var subQ3=sQuery(id+"F4.wireOp",EDGE,"E68.0.2");Q6=makeQuery(id+"F4.imprint","IMPRINT",FACE,{"disambiguationData":[TD([[makeQuery(id+"F4.imprint","IMPRINT",EDGE,{"derivedFrom":subQ3}),1.0]])]});}
            var Q7;
            {var subQ3=sQuery(id+"F4.wireOp",EDGE,"E67.0.2");Q7=makeQuery(id+"F4.imprint","IMPRINT",FACE,{"disambiguationData":[TD([[makeQuery(id+"F4.imprint","IMPRINT",EDGE,{"derivedFrom":subQ3}),1.0]])]});}
            var Q8;
            {var subQ3=sQuery(id+"F4.wireOp",EDGE,"E64.0.2");Q8=makeQuery(id+"F4.imprint","IMPRINT",FACE,{"disambiguationData":[TD([[makeQuery(id+"F4.imprint","IMPRINT",EDGE,{"derivedFrom":subQ3}),1.0]])]});}
            var Q9;
            {var subQ3=sQuery(id+"F4.wireOp",EDGE,"E63.0.2");Q9=makeQuery(id+"F4.imprint","IMPRINT",FACE,{"disambiguationData":[TD([[makeQuery(id+"F4.imprint","IMPRINT",EDGE,{"derivedFrom":subQ3}),1.0]])]});}
            var Q10;
            Q10=makeQuery(id+"F4.imprint","IMPRINT",FACE,{"disambiguationData":[TD([[makeQuery(id+"F4.imprint","IMPRINT",EDGE,{"derivedFrom":sQuery(id+"F4.wireOp",EDGE,"E65.0.2")}),1.0]])]});
            var Q11;
            Q11=makeQuery(id+"F4.imprint","IMPRINT",FACE,{"disambiguationData":[TD([[makeQuery(id+"F4.imprint","IMPRINT",EDGE,{"derivedFrom":sQuery(id+"F4.wireOp",EDGE,"E66.0.2")}),1.0]])]});
            var Q12;
            {var subQ2=sQuery(id+"F4.wireOp",EDGE,"E75.bottom");Q12=makeQuery(id+"F4.imprint","IMPRINT",FACE,{"disambiguationData":[TD([[makeQuery(id+"F4.imprint","IMPRINT",EDGE,{"derivedFrom":subQ2}),-1.0]])]});}
            var Q13;
            {var subQ2=sQuery(id+"F4.wireOp",EDGE,"E74.bottom");Q13=makeQuery(id+"F4.imprint","IMPRINT",FACE,{"disambiguationData":[TD([[makeQuery(id+"F4.imprint","IMPRINT",EDGE,{"derivedFrom":subQ2}),-1.0]])]});}
            extrude(context, id + "F5", {"entities" : qUnion([Q0, Q1, Q2, Q3, Q4, Q5, Q6, Q7, Q8, Q9, Q10, Q11, Q12, Q13]), "oppositeDirection" : true, "depth" : 3 * mm});
        }
        {
            var Q0;
            Q0=makeQuery(id+"F1.opExtrude","SWEPT_FACE",FACE,{"disambiguationData":[OSD([sQuery(id+"F0.wireOp",EDGE,"E18.top")])]});
            var sketch = newSketch(context, id + "F6", { "sketchPlane" : qUnion([Q0])});
            skLineSegment(sketch, "E93.bottom", {"start": v(58.5, -3) * mm, "end": v(8.5, -3) * mm});
            skLineSegment(sketch, "E93.top", {"start": v(48.5, 15) * mm, "end": v(18.5, 15) * mm});
            skLineSegment(sketch, "E93.left", {"start": v(58.5, -3) * mm, "end": v(58.5, 5) * mm});
            skLineSegment(sketch, "E93.right", {"start": v(8.5, -3) * mm, "end": v(8.5, 5) * mm});
            skLineSegment(sketch, "E94", {"start": v(58.5, -3) * mm, "end": v(48.5, -3) * mm, "construction": true});
            skLineSegment(sketch, "E95", {"start": v(48.5, -3) * mm, "end": v(58.5, -3) * mm, "construction": true});
            skLineSegment(sketch, "E96.0.0", {"start": v(28.5, 0) * mm, "end": v(18.5, 0) * mm, "construction": true});
            skLineSegment(sketch, "E96.0.1", {"start": v(18.5, 0) * mm, "end": v(18.5, -3) * mm, "construction": true});
            skLineSegment(sketch, "E96.0.2", {"start": v(18.5, -3) * mm, "end": v(28.5, -3) * mm, "construction": true});
            skLineSegment(sketch, "E96.0.3", {"start": v(28.5, -3) * mm, "end": v(28.5, 0) * mm, "construction": true});
            skLineSegment(sketch, "E97.0.0", {"start": v(48.5, 0) * mm, "end": v(38.5, 0) * mm, "construction": true});
            skLineSegment(sketch, "E97.0.1", {"start": v(38.5, 0) * mm, "end": v(38.5, -3) * mm, "construction": true});
            skLineSegment(sketch, "E97.0.2", {"start": v(38.5, -3) * mm, "end": v(48.5, -3) * mm, "construction": true});
            skLineSegment(sketch, "E97.0.3", {"start": v(48.5, -3) * mm, "end": v(48.5, 0) * mm, "construction": true});
            skLineSegment(sketch, "E98", {"start": v(8.5, -3) * mm, "end": v(18.5, -3) * mm, "construction": true});
            skPoint(sketch, "E99.visualSharp", {"position": v(8.5, 15) * mm});
            skArc(sketch, "E99.filletArc", {"start": v(18.5, 15) * mm, "mid": v(11.43, 12.07) * mm, "end": v(8.5, 5) * mm});
            skPoint(sketch, "E100.visualSharp", {"position": v(58.5, 15) * mm});
            skArc(sketch, "E100.filletArc", {"start": v(58.5, 5) * mm, "mid": v(55.57, 12.07) * mm, "end": v(48.5, 15) * mm});
            skLineSegment(sketch, "E101.0.0", {"start": v(28.5, 0) * mm, "end": v(18.5, 0) * mm});
            skLineSegment(sketch, "E101.0.1", {"start": v(18.5, 0) * mm, "end": v(18.5, -3) * mm});
            skLineSegment(sketch, "E101.0.2", {"start": v(18.5, -3) * mm, "end": v(28.5, -3) * mm});
            skLineSegment(sketch, "E101.0.3", {"start": v(28.5, -3) * mm, "end": v(28.5, 0) * mm});
            skLineSegment(sketch, "E102", {"start": v(48.5, 0) * mm, "end": v(58.5, 0) * mm});
            skLineSegment(sketch, "E103", {"start": v(38.5, 0) * mm, "end": v(28.5, 0) * mm});
            skLineSegment(sketch, "E104", {"start": v(18.5, 0) * mm, "end": v(8.5, 0) * mm});
            skSolve(sketch);
        }
        {
            var Q0;
            Q0=makeQuery(id+"F6.imprint","IMPRINT",FACE,{"disambiguationData":[TD([[makeQuery(id+"F6.imprint","IMPRINT",EDGE,{"derivedFrom":sQuery(id+"F6.wireOp",EDGE,"E93.top")}),1.0]])]});
            var Q1;
            Q1=makeQuery(id+"F6.imprint","IMPRINT",FACE,{"disambiguationData":[TD([[makeQuery(id+"F6.imprint","IMPRINT",EDGE,{"derivedFrom":sQuery(id+"F6.wireOp",EDGE,"E101.0.0")}),1.0]])]});
            var Q2;
            {var subQ0=sQuery(id+"F0.wireOp",EDGE,"E18.top");Q2=makeQuery(id+"F6.imprint","IMPRINT",FACE,{"disambiguationData":[TD([[makeQuery(id+"F6.imprint","IMPRINT",EDGE,{"derivedFrom":makeQuery(id+"F1.opExtrude","CAP_EDGE",EDGE,{"disambiguationData":[OSD([subQ0])],"isStart":true})}),1.0]])]});}
            extrude(context, id + "F7", {"entities" : qUnion([Q0, Q1, Q2]), "depth" : 3 * mm});
        }
        {
            var Q0;
            Q0=makeQuery(id+"F1.opExtrude","CAP_FACE",FACE,{"disambiguationData":[OSD([sQuery(id+"F0.wireOp",EDGE,"E0.top"),sQuery(id+"F0.wireOp",EDGE,"E0.left"),sQuery(id+"F0.wireOp",EDGE,"E0.right"),sQuery(id+"F0.wireOp",EDGE,"E1.bottom"),sQuery(id+"F0.wireOp",EDGE,"E1.left"),sQuery(id+"F0.wireOp",EDGE,"E1.right"),sQuery(id+"F0.wireOp",EDGE,"E2.bottom"),sQuery(id+"F0.wireOp",EDGE,"E2.left"),sQuery(id+"F0.wireOp",EDGE,"E2.right"),sQuery(id+"F0.wireOp",EDGE,"E3.bottom"),sQuery(id+"F0.wireOp",EDGE,"E3.left"),sQuery(id+"F0.wireOp",EDGE,"E3.right"),sQuery(id+"F0.wireOp",EDGE,"E4.bottom"),sQuery(id+"F0.wireOp",EDGE,"E4.left"),sQuery(id+"F0.wireOp",EDGE,"E4.right"),sQuery(id+"F0.wireOp",EDGE,"E5.bottom"),sQuery(id+"F0.wireOp",EDGE,"E5.left"),sQuery(id+"F0.wireOp",EDGE,"E5.right"),sQuery(id+"F0.wireOp",EDGE,"E6.bottom"),sQuery(id+"F0.wireOp",EDGE,"E6.top"),sQuery(id+"F0.wireOp",EDGE,"E6.right"),sQuery(id+"F0.wireOp",EDGE,"E7.bottom"),sQuery(id+"F0.wireOp",EDGE,"E7.top"),sQuery(id+"F0.wireOp",EDGE,"E7.right"),sQuery(id+"F0.wireOp",EDGE,"E8.bottom"),sQuery(id+"F0.wireOp",EDGE,"E8.top"),sQuery(id+"F0.wireOp",EDGE,"E8.right"),sQuery(id+"F0.wireOp",EDGE,"E9.bottom"),sQuery(id+"F0.wireOp",EDGE,"E9.top"),sQuery(id+"F0.wireOp",EDGE,"E9.right"),sQuery(id+"F0.wireOp",EDGE,"E11"),sQuery(id+"F0.wireOp",EDGE,"E12"),sQuery(id+"F0.wireOp",EDGE,"E13"),sQuery(id+"F0.wireOp",EDGE,"E14"),sQuery(id+"F0.wireOp",EDGE,"E16"),sQuery(id+"F0.wireOp",EDGE,"E17"),sQuery(id+"F0.wireOp",EDGE,"E18.bottom"),sQuery(id+"F0.wireOp",EDGE,"E18.top"),sQuery(id+"F0.wireOp",EDGE,"E18.left"),sQuery(id+"F0.wireOp",EDGE,"E18.right"),sQuery(id+"F0.wireOp",EDGE,"E19.bottom"),sQuery(id+"F0.wireOp",EDGE,"E19.top"),sQuery(id+"F0.wireOp",EDGE,"E19.left"),sQuery(id+"F0.wireOp",EDGE,"E19.right")])],"isStart":true});
            var sketch = newSketch(context, id + "F8", { "sketchPlane" : qUnion([Q0])});
            skLineSegment(sketch, "E105.0.0", {"start": v(0, 28.5) * mm, "end": v(-67, 28.5) * mm});
            skLineSegment(sketch, "E105.0.1", {"start": v(-67, 28.5) * mm, "end": v(-67, 23.5) * mm});
            skLineSegment(sketch, "E105.0.2", {"start": v(-67, 23.5) * mm, "end": v(-64, 23.5) * mm});
            skLineSegment(sketch, "E105.0.3", {"start": v(-64, 23.5) * mm, "end": v(-64, 17.5) * mm});
            skLineSegment(sketch, "E105.0.4", {"start": v(-64, 17.5) * mm, "end": v(-67, 17.5) * mm});
            skLineSegment(sketch, "E105.0.5", {"start": v(-67, 17.5) * mm, "end": v(-67, 11.5) * mm});
            skLineSegment(sketch, "E105.0.6", {"start": v(-67, 11.5) * mm, "end": v(-64, 11.5) * mm});
            skLineSegment(sketch, "E105.0.7", {"start": v(-64, 11.5) * mm, "end": v(-64, 5.5) * mm});
            skLineSegment(sketch, "E105.0.8", {"start": v(-64, 5.5) * mm, "end": v(-67, 5.5) * mm});
            skLineSegment(sketch, "E105.0.9", {"start": v(-67, 5.5) * mm, "end": v(-67, 3) * mm});
            skLineSegment(sketch, "E105.0.10", {"start": v(-67, 3) * mm, "end": v(-60.5, 3) * mm});
            skLineSegment(sketch, "E105.0.11", {"start": v(-60.5, 3) * mm, "end": v(-60.5, 0) * mm});
            skLineSegment(sketch, "E105.0.12", {"start": v(-60.5, 0) * mm, "end": v(-54.5, 0) * mm});
            skLineSegment(sketch, "E105.0.13", {"start": v(-54.5, 0) * mm, "end": v(-54.5, 3) * mm});
            skLineSegment(sketch, "E105.0.14", {"start": v(-54.5, 3) * mm, "end": v(-48.5, 3) * mm});
            skLineSegment(sketch, "E105.0.15", {"start": v(-48.5, 3) * mm, "end": v(-48.5, 0) * mm});
            skLineSegment(sketch, "E105.0.16", {"start": v(-48.5, 0) * mm, "end": v(-42.5, 0) * mm});
            skLineSegment(sketch, "E105.0.17", {"start": v(-42.5, 0) * mm, "end": v(-42.5, 3) * mm});
            skLineSegment(sketch, "E105.0.18", {"start": v(-42.5, 3) * mm, "end": v(-36.5, 3) * mm});
            skLineSegment(sketch, "E105.0.19", {"start": v(-36.5, 3) * mm, "end": v(-36.5, 0) * mm});
            skLineSegment(sketch, "E105.0.20", {"start": v(-36.5, 0) * mm, "end": v(-30.5, 0) * mm});
            skLineSegment(sketch, "E105.0.21", {"start": v(-30.5, 0) * mm, "end": v(-30.5, 3) * mm});
            skLineSegment(sketch, "E105.0.22", {"start": v(-30.5, 3) * mm, "end": v(-24.5, 3) * mm});
            skLineSegment(sketch, "E105.0.23", {"start": v(-24.5, 3) * mm, "end": v(-24.5, 0) * mm});
            skLineSegment(sketch, "E105.0.24", {"start": v(-24.5, 0) * mm, "end": v(-18.5, 0) * mm});
            skLineSegment(sketch, "E105.0.25", {"start": v(-18.5, 0) * mm, "end": v(-18.5, 3) * mm});
            skLineSegment(sketch, "E105.0.26", {"start": v(-18.5, 3) * mm, "end": v(-12.5, 3) * mm});
            skLineSegment(sketch, "E105.0.27", {"start": v(-12.5, 3) * mm, "end": v(-12.5, 0) * mm});
            skLineSegment(sketch, "E105.0.28", {"start": v(-12.5, 0) * mm, "end": v(-6.5, 0) * mm});
            skLineSegment(sketch, "E105.0.29", {"start": v(-6.5, 0) * mm, "end": v(-6.5, 3) * mm});
            skLineSegment(sketch, "E105.0.30", {"start": v(-6.5, 3) * mm, "end": v(0, 3) * mm});
            skLineSegment(sketch, "E105.0.31", {"start": v(0, 3) * mm, "end": v(0, 5.5) * mm});
            skLineSegment(sketch, "E105.0.32", {"start": v(0, 5.5) * mm, "end": v(-3, 5.5) * mm});
            skLineSegment(sketch, "E105.0.33", {"start": v(-3, 5.5) * mm, "end": v(-3, 11.5) * mm});
            skLineSegment(sketch, "E105.0.34", {"start": v(-3, 11.5) * mm, "end": v(0, 11.5) * mm});
            skLineSegment(sketch, "E105.0.35", {"start": v(0, 11.5) * mm, "end": v(0, 17.5) * mm});
            skLineSegment(sketch, "E105.0.36", {"start": v(0, 17.5) * mm, "end": v(-3, 17.5) * mm});
            skLineSegment(sketch, "E105.0.37", {"start": v(-3, 17.5) * mm, "end": v(-3, 23.5) * mm});
            skLineSegment(sketch, "E105.0.38", {"start": v(-3, 23.5) * mm, "end": v(0, 23.5) * mm});
            skLineSegment(sketch, "E105.0.39", {"start": v(0, 23.5) * mm, "end": v(0, 28.5) * mm});
            skLineSegment(sketch, "E106.bottom", {"start": v(-67, 28.5) * mm, "end": v(0, 28.5) * mm});
            skLineSegment(sketch, "E106.top", {"start": v(-67, 0) * mm, "end": v(0, 0) * mm});
            skLineSegment(sketch, "E106.left", {"start": v(-67, 28.5) * mm, "end": v(-67, 0) * mm});
            skLineSegment(sketch, "E106.right", {"start": v(0, 28.5) * mm, "end": v(0, 0) * mm});
            skLineSegment(sketch, "E107.0.0", {"start": v(-48.5, 10.1) * mm, "end": v(-58.5, 10.1) * mm});
            skLineSegment(sketch, "E107.0.2", {"start": v(-58.5, 10.1) * mm, "end": v(-48.5, 10.1) * mm});
            skLineSegment(sketch, "E107.0.4", {"start": v(-48.5, 10.1) * mm, "end": v(-38.5, 10.1) * mm});
            skLineSegment(sketch, "E107.0.6", {"start": v(-38.5, 10.1) * mm, "end": v(-28.5, 10.1) * mm});
            skLineSegment(sketch, "E107.0.8", {"start": v(-28.5, 10.1) * mm, "end": v(-18.5, 10.1) * mm});
            skLineSegment(sketch, "E107.0.10", {"start": v(-18.5, 10.1) * mm, "end": v(-8.5, 10.1) * mm});
            skLineSegment(sketch, "E107.0.12", {"start": v(-8.5, 10.1) * mm, "end": v(-18.5, 10.1) * mm});
            skLineSegment(sketch, "E107.0.13", {"start": v(-18.5, 10.1) * mm, "end": v(-48.5, 10.1) * mm});
            skLineSegment(sketch, "E108.0.0", {"start": v(-58.5, 13.1) * mm, "end": v(-48.5, 13.1) * mm});
            skLineSegment(sketch, "E108.0.1", {"start": v(-48.5, 13.1) * mm, "end": v(-18.5, 13.1) * mm});
            skLineSegment(sketch, "E108.0.2", {"start": v(-18.5, 13.1) * mm, "end": v(-8.5, 13.1) * mm});
            skLineSegment(sketch, "E108.0.4", {"start": v(-8.5, 13.1) * mm, "end": v(-18.5, 13.1) * mm});
            skLineSegment(sketch, "E108.0.6", {"start": v(-18.5, 13.1) * mm, "end": v(-28.5, 13.1) * mm});
            skLineSegment(sketch, "E108.0.8", {"start": v(-28.5, 13.1) * mm, "end": v(-38.5, 13.1) * mm});
            skLineSegment(sketch, "E108.0.10", {"start": v(-38.5, 13.1) * mm, "end": v(-48.5, 13.1) * mm});
            skLineSegment(sketch, "E108.0.12", {"start": v(-48.5, 13.1) * mm, "end": v(-58.5, 13.1) * mm});
            skLineSegment(sketch, "E109.bottom", {"start": v(-58.5, 13.1) * mm, "end": v(-58.5, 13.1) * mm});
            skLineSegment(sketch, "E109.top", {"start": v(-58.5, 10.1) * mm, "end": v(-58.5, 10.1) * mm});
            skLineSegment(sketch, "E109.left", {"start": v(-58.5, 13.1) * mm, "end": v(-58.5, 10.1) * mm});
            skLineSegment(sketch, "E109.right", {"start": v(-58.5, 13.1) * mm, "end": v(-58.5, 10.1) * mm});
            skLineSegment(sketch, "E110.bottom", {"start": v(-8.5, 13.1) * mm, "end": v(-8.5, 13.1) * mm});
            skLineSegment(sketch, "E110.top", {"start": v(-8.5, 10.1) * mm, "end": v(-8.5, 10.1) * mm});
            skLineSegment(sketch, "E110.left", {"start": v(-8.5, 13.1) * mm, "end": v(-8.5, 10.1) * mm});
            skLineSegment(sketch, "E110.right", {"start": v(-8.5, 13.1) * mm, "end": v(-8.5, 10.1) * mm});
            skSolve(sketch);
        }
        {
            var Q0;
            Q0=makeQuery(id+"F5.opExtrude","CAP_FACE",FACE,{"disambiguationData":[OSD([sQuery(id+"F4.wireOp",EDGE,"E74.bottom"),sQuery(id+"F4.wireOp",EDGE,"E74.top"),sQuery(id+"F4.wireOp",EDGE,"E75.bottom"),sQuery(id+"F4.wireOp",EDGE,"E75.top"),sQuery(id+"F4.wireOp",EDGE,"E76.bottom"),sQuery(id+"F4.wireOp",EDGE,"E76.top"),sQuery(id+"F4.wireOp",EDGE,"E76.left"),sQuery(id+"F4.wireOp",EDGE,"E76.right"),sQuery(id+"F4.wireOp",EDGE,"E77.0.1"),sQuery(id+"F4.wireOp",EDGE,"E77.0.2"),sQuery(id+"F4.wireOp",EDGE,"E77.0.3"),sQuery(id+"F4.wireOp",EDGE,"E78.0.1"),sQuery(id+"F4.wireOp",EDGE,"E78.0.2"),sQuery(id+"F4.wireOp",EDGE,"E78.0.3"),sQuery(id+"F4.wireOp",EDGE,"E79.0.1"),sQuery(id+"F4.wireOp",EDGE,"E79.0.2"),sQuery(id+"F4.wireOp",EDGE,"E79.0.3"),sQuery(id+"F4.wireOp",EDGE,"E80.0.1"),sQuery(id+"F4.wireOp",EDGE,"E80.0.2"),sQuery(id+"F4.wireOp",EDGE,"E80.0.3"),sQuery(id+"F4.wireOp",EDGE,"E82.0.1"),sQuery(id+"F4.wireOp",EDGE,"E82.0.2"),sQuery(id+"F4.wireOp",EDGE,"E82.0.3"),sQuery(id+"F4.wireOp",EDGE,"E83.0.2"),sQuery(id+"F4.wireOp",EDGE,"E83.0.3"),sQuery(id+"F4.wireOp",EDGE,"E81.0.2"),sQuery(id+"F4.wireOp",EDGE,"E81.0.3"),sQuery(id+"F4.wireOp",EDGE,"E84.0.1"),sQuery(id+"F4.wireOp",EDGE,"E84.0.2"),sQuery(id+"F4.wireOp",EDGE,"E85.0.1"),sQuery(id+"F4.wireOp",EDGE,"E85.0.2"),sQuery(id+"F4.wireOp",EDGE,"E85.0.3"),sQuery(id+"F4.wireOp",EDGE,"E86.0.1"),sQuery(id+"F4.wireOp",EDGE,"E86.0.2"),sQuery(id+"F4.wireOp",EDGE,"E86.0.3"),sQuery(id+"F4.wireOp",EDGE,"E87.0.1"),sQuery(id+"F4.wireOp",EDGE,"E87.0.2"),sQuery(id+"F4.wireOp",EDGE,"E87.0.3"),sQuery(id+"F4.wireOp",EDGE,"E88.0.1"),sQuery(id+"F4.wireOp",EDGE,"E88.0.2"),sQuery(id+"F4.wireOp",EDGE,"E88.0.3"),sQuery(id+"F4.wireOp",EDGE,"E89.0.1"),sQuery(id+"F4.wireOp",EDGE,"E89.0.2"),sQuery(id+"F4.wireOp",EDGE,"E90"),sQuery(id+"F4.wireOp",EDGE,"E91"),sQuery(id+"F4.wireOp",EDGE,"E92")])],"isStart":true});
            var sketch = newSketch(context, id + "F9", { "sketchPlane" : qUnion([Q0])});
            skLineSegment(sketch, "E111.bottom", {"start": v(-30.4, 28.5) * mm, "end": v(-33.6, 28.5) * mm});
            skLineSegment(sketch, "E111.top", {"start": v(-30.4, 24.5) * mm, "end": v(-33.6, 24.5) * mm});
            skLineSegment(sketch, "E111.left", {"start": v(-30.4, 28.5) * mm, "end": v(-30.4, 24.5) * mm});
            skLineSegment(sketch, "E111.right", {"start": v(-33.6, 28.5) * mm, "end": v(-33.6, 24.5) * mm});
            skLineSegment(sketch, "E112.bottom", {"start": v(-115.8, 28.5) * mm, "end": v(-119, 28.5) * mm});
            skLineSegment(sketch, "E112.top", {"start": v(-115.8, 24.5) * mm, "end": v(-119, 24.5) * mm});
            skLineSegment(sketch, "E112.left", {"start": v(-115.8, 28.5) * mm, "end": v(-115.8, 24.5) * mm});
            skLineSegment(sketch, "E112.right", {"start": v(-119, 28.5) * mm, "end": v(-119, 24.5) * mm});
            skLineSegment(sketch, "E113.bottom", {"start": v(-88.4, 28.5) * mm, "end": v(-85.2, 28.5) * mm});
            skLineSegment(sketch, "E113.top", {"start": v(-88.4, 24.5) * mm, "end": v(-85.2, 24.5) * mm});
            skLineSegment(sketch, "E113.left", {"start": v(-88.4, 28.5) * mm, "end": v(-88.4, 24.5) * mm});
            skLineSegment(sketch, "E113.right", {"start": v(-85.2, 28.5) * mm, "end": v(-85.2, 24.5) * mm});
            skLineSegment(sketch, "E114.bottom", {"start": v(-61, 28.5) * mm, "end": v(-57.8, 28.5) * mm});
            skLineSegment(sketch, "E114.top", {"start": v(-61, 24.5) * mm, "end": v(-57.8, 24.5) * mm});
            skLineSegment(sketch, "E114.left", {"start": v(-57.8, 28.5) * mm, "end": v(-57.8, 24.5) * mm});
            skLineSegment(sketch, "E114.right", {"start": v(-61, 28.5) * mm, "end": v(-61, 24.5) * mm});
            skLineSegment(sketch, "E115.bottom", {"start": v(-146.4, 28.5) * mm, "end": v(-149.6, 28.5) * mm});
            skLineSegment(sketch, "E115.top", {"start": v(-146.4, 24.5) * mm, "end": v(-149.6, 24.5) * mm});
            skLineSegment(sketch, "E115.left", {"start": v(-146.4, 28.5) * mm, "end": v(-146.4, 24.5) * mm});
            skLineSegment(sketch, "E115.right", {"start": v(-149.6, 28.5) * mm, "end": v(-149.6, 24.5) * mm});
            skLineSegment(sketch, "E116.bottom", {"start": v(-146.4, 24.5) * mm, "end": v(-119, 24.5) * mm, "construction": true});
            skLineSegment(sketch, "E116.top", {"start": v(-146.4, 24.5) * mm, "end": v(-119, 24.5) * mm, "construction": true});
            skLineSegment(sketch, "E116.left", {"start": v(-146.4, 24.5) * mm, "end": v(-146.4, 24.5) * mm});
            skLineSegment(sketch, "E116.right", {"start": v(-119, 24.5) * mm, "end": v(-119, 24.5) * mm});
            skLineSegment(sketch, "E117.bottom", {"start": v(-115.8, 24.5) * mm, "end": v(-88.4, 24.5) * mm, "construction": true});
            skLineSegment(sketch, "E117.top", {"start": v(-115.8, 24.5) * mm, "end": v(-88.4, 24.5) * mm, "construction": true});
            skLineSegment(sketch, "E117.left", {"start": v(-115.8, 24.5) * mm, "end": v(-115.8, 24.5) * mm});
            skLineSegment(sketch, "E117.right", {"start": v(-88.4, 24.5) * mm, "end": v(-88.4, 24.5) * mm});
            skLineSegment(sketch, "E118.bottom", {"start": v(-85.2, 24.5) * mm, "end": v(-57.8, 24.5) * mm, "construction": true});
            skLineSegment(sketch, "E118.top", {"start": v(-85.2, 24.5) * mm, "end": v(-57.8, 24.5) * mm, "construction": true});
            skLineSegment(sketch, "E118.left", {"start": v(-85.2, 24.5) * mm, "end": v(-85.2, 24.5) * mm});
            skLineSegment(sketch, "E118.right", {"start": v(-57.8, 24.5) * mm, "end": v(-57.8, 24.5) * mm});
            skLineSegment(sketch, "E119.bottom", {"start": v(-61, 24.5) * mm, "end": v(-33.6, 24.5) * mm, "construction": true});
            skLineSegment(sketch, "E119.top", {"start": v(-61, 24.5) * mm, "end": v(-33.6, 24.5) * mm, "construction": true});
            skLineSegment(sketch, "E119.left", {"start": v(-61, 24.5) * mm, "end": v(-61, 24.5) * mm});
            skLineSegment(sketch, "E119.right", {"start": v(-33.6, 24.5) * mm, "end": v(-33.6, 24.5) * mm});
            skLineSegment(sketch, "E120.bottom", {"start": v(-132.7, 24.5) * mm, "end": v(-102.1, 24.5) * mm, "construction": true});
            skLineSegment(sketch, "E120.top", {"start": v(-132.7, 24.5) * mm, "end": v(-102.1, 24.5) * mm, "construction": true});
            skLineSegment(sketch, "E120.left", {"start": v(-132.7, 24.5) * mm, "end": v(-132.7, 24.5) * mm});
            skLineSegment(sketch, "E120.right", {"start": v(-102.1, 24.5) * mm, "end": v(-102.1, 24.5) * mm});
            skLineSegment(sketch, "E121", {"start": v(-149.6, 24.5) * mm, "end": v(-177, 24.5) * mm, "construction": true});
            skLineSegment(sketch, "E122", {"start": v(-30.4, 24.5) * mm, "end": v(-3, 24.5) * mm, "construction": true});
            skSolve(sketch);
        }
        {
            var Q0;
            Q0=makeQuery(id+"F9.imprint","IMPRINT",FACE,{"disambiguationData":[TD([[makeQuery(id+"F9.imprint","IMPRINT",EDGE,{"derivedFrom":sQuery(id+"F9.wireOp",EDGE,"E115.bottom")}),1.0]])]});
            var Q1;
            Q1=makeQuery(id+"F9.imprint","IMPRINT",FACE,{"disambiguationData":[TD([[makeQuery(id+"F9.imprint","IMPRINT",EDGE,{"derivedFrom":sQuery(id+"F9.wireOp",EDGE,"E112.bottom")}),1.0]])]});
            var Q2;
            Q2=makeQuery(id+"F9.imprint","IMPRINT",FACE,{"disambiguationData":[TD([[makeQuery(id+"F9.imprint","IMPRINT",EDGE,{"derivedFrom":sQuery(id+"F9.wireOp",EDGE,"E113.bottom")}),1.0]])]});
            var Q3;
            Q3=makeQuery(id+"F9.imprint","IMPRINT",FACE,{"disambiguationData":[TD([[makeQuery(id+"F9.imprint","IMPRINT",EDGE,{"derivedFrom":sQuery(id+"F9.wireOp",EDGE,"E114.bottom")}),1.0]])]});
            var Q4;
            Q4=makeQuery(id+"F9.imprint","IMPRINT",FACE,{"disambiguationData":[TD([[makeQuery(id+"F9.imprint","IMPRINT",EDGE,{"derivedFrom":sQuery(id+"F9.wireOp",EDGE,"E111.bottom")}),1.0]])]});
            extrude(context, id + "F10", {"entities" : qUnion([Q0, Q1, Q2, Q3, Q4]), "operationType" : NewBodyOperationType.REMOVE, "endBound" : BoundingType.THROUGH_ALL, "oppositeDirection" : true, "depth" : 25 * mm});
        }
        {
            var Q0;
            Q0=makeQuery(id+"F10.boolean.opBoolean","COPY",FACE,{"derivedFrom":makeQuery(id+"F10.opExtrude","SWEPT_FACE",FACE,{"disambiguationData":[OSD([sQuery(id+"F9.wireOp",EDGE,"E111.right")])]})});
            var sketch = newSketch(context, id + "F11", { "sketchPlane" : qUnion([Q0])});
            skLineSegment(sketch, "E123.0.0", {"start": v(-64, 28.5) * mm, "end": v(-67, 28.5) * mm});
            skLineSegment(sketch, "E123.0.1", {"start": v(-67, 28.5) * mm, "end": v(-67, 24.5) * mm});
            skLineSegment(sketch, "E123.0.2", {"start": v(-67, 24.5) * mm, "end": v(-64, 24.5) * mm});
            skLineSegment(sketch, "E123.0.3", {"start": v(-64, 24.5) * mm, "end": v(-64, 28.5) * mm});
            skLineSegment(sketch, "E124.bottom", {"start": v(-64, 28.5) * mm, "end": v(0, 28.5) * mm});
            skLineSegment(sketch, "E124.top", {"start": v(-64, 3) * mm, "end": v(0, 3) * mm});
            skLineSegment(sketch, "E124.left", {"start": v(-64, 28.5) * mm, "end": v(-64, 3) * mm});
            skLineSegment(sketch, "E124.right", {"start": v(0, 28.5) * mm, "end": v(0, 3) * mm});
            skLineSegment(sketch, "E125.bottom", {"start": v(0, 28.5) * mm, "end": v(3, 28.5) * mm});
            skLineSegment(sketch, "E125.top", {"start": v(0, 24.5) * mm, "end": v(3, 24.5) * mm});
            skLineSegment(sketch, "E125.left", {"start": v(0, 28.5) * mm, "end": v(0, 24.5) * mm});
            skLineSegment(sketch, "E125.right", {"start": v(3, 28.5) * mm, "end": v(3, 24.5) * mm});
            skLineSegment(sketch, "E126", {"start": v(-66.5, 25) * mm, "end": v(-64, 25) * mm});
            skLineSegment(sketch, "E127", {"start": v(-66.5, 28.57) * mm, "end": v(-66.5, 25) * mm});
            skLineSegment(sketch, "E128", {"start": v(0, 25) * mm, "end": v(2.5, 25) * mm});
            skLineSegment(sketch, "E129", {"start": v(2.5, 28.5) * mm, "end": v(2.5, 25) * mm});
            skLineSegment(sketch, "E130.trimOffspring", {"start": v(3, 25) * mm, "end": v(3.01, 25) * mm});
            skSolve(sketch);
        }
        {
            var Q0;
            {var subQ6=sQuery(id+"F11.wireOp",EDGE,"E124.bottom");Q0=makeQuery(id+"F11.imprint","IMPRINT",FACE,{"disambiguationData":[TD([[makeQuery(id+"F11.imprint","IMPRINT",EDGE,{"derivedFrom":subQ6}),-1.0]])]});}
            var Q1;
            {var subQ1=sQuery(id+"F11.wireOp",EDGE,"E128");Q1=makeQuery(id+"F11.imprint","IMPRINT",FACE,{"disambiguationData":[TD([[makeQuery(id+"F11.imprint","IMPRINT",EDGE,{"derivedFrom":subQ1}),1.0]])]});}
            var Q2;
            {var subQ3=sQuery(id+"F11.wireOp",EDGE,"E126");Q2=makeQuery(id+"F11.imprint","IMPRINT",FACE,{"disambiguationData":[TD([[makeQuery(id+"F11.imprint","IMPRINT",EDGE,{"derivedFrom":subQ3}),1.0]])]});}
            extrude(context, id + "F12", {"entities" : qUnion([Q0, Q1, Q2]), "depth" : 3 * mm});
        }
        {
            var Q0;
            {var subQ26=sQuery(id+"F8.wireOp",EDGE,"E105.0.2");Q0=makeQuery(id+"F8.imprint","IMPRINT",FACE,{"disambiguationData":[TD([[makeQuery(id+"F8.imprint","IMPRINT",EDGE,{"derivedFrom":subQ26}),1.0]])]});}
            var Q1;
            {var subQ2=sQuery(id+"F8.wireOp",EDGE,"E105.0.2");Q1=makeQuery(id+"F8.imprint","IMPRINT",FACE,{"disambiguationData":[TD([[makeQuery(id+"F8.imprint","IMPRINT",EDGE,{"derivedFrom":subQ2}),-1.0]])]});}
            var Q2;
            {var subQ2=sQuery(id+"F8.wireOp",EDGE,"E105.0.6");Q2=makeQuery(id+"F8.imprint","IMPRINT",FACE,{"disambiguationData":[TD([[makeQuery(id+"F8.imprint","IMPRINT",EDGE,{"derivedFrom":subQ2}),-1.0]])]});}
            var Q3;
            {var subQ1=sQuery(id+"F8.wireOp",EDGE,"E105.0.36");Q3=makeQuery(id+"F8.imprint","IMPRINT",FACE,{"disambiguationData":[TD([[makeQuery(id+"F8.imprint","IMPRINT",EDGE,{"derivedFrom":subQ1}),-1.0]])]});}
            var Q4;
            {var subQ1=sQuery(id+"F8.wireOp",EDGE,"E105.0.32");Q4=makeQuery(id+"F8.imprint","IMPRINT",FACE,{"disambiguationData":[TD([[makeQuery(id+"F8.imprint","IMPRINT",EDGE,{"derivedFrom":subQ1}),-1.0]])]});}
            var Q5;
            {var subQ4=sQuery(id+"F8.wireOp",EDGE,"E105.0.29");Q5=makeQuery(id+"F8.imprint","IMPRINT",FACE,{"disambiguationData":[TD([[makeQuery(id+"F8.imprint","IMPRINT",EDGE,{"derivedFrom":subQ4}),-1.0]])]});}
            var Q6;
            {var subQ1=sQuery(id+"F8.wireOp",EDGE,"E105.0.25");Q6=makeQuery(id+"F8.imprint","IMPRINT",FACE,{"disambiguationData":[TD([[makeQuery(id+"F8.imprint","IMPRINT",EDGE,{"derivedFrom":subQ1}),-1.0]])]});}
            var Q7;
            {var subQ2=sQuery(id+"F8.wireOp",EDGE,"E105.0.21");Q7=makeQuery(id+"F8.imprint","IMPRINT",FACE,{"disambiguationData":[TD([[makeQuery(id+"F8.imprint","IMPRINT",EDGE,{"derivedFrom":subQ2}),-1.0]])]});}
            var Q8;
            {var subQ1=sQuery(id+"F8.wireOp",EDGE,"E105.0.17");Q8=makeQuery(id+"F8.imprint","IMPRINT",FACE,{"disambiguationData":[TD([[makeQuery(id+"F8.imprint","IMPRINT",EDGE,{"derivedFrom":subQ1}),-1.0]])]});}
            var Q9;
            {var subQ1=sQuery(id+"F8.wireOp",EDGE,"E105.0.13");Q9=makeQuery(id+"F8.imprint","IMPRINT",FACE,{"disambiguationData":[TD([[makeQuery(id+"F8.imprint","IMPRINT",EDGE,{"derivedFrom":subQ1}),-1.0]])]});}
            var Q10;
            {var subQ3=sQuery(id+"F8.wireOp",EDGE,"E105.0.10");Q10=makeQuery(id+"F8.imprint","IMPRINT",FACE,{"disambiguationData":[TD([[makeQuery(id+"F8.imprint","IMPRINT",EDGE,{"derivedFrom":subQ3}),1.0]])]});}
            extrude(context, id + "F13", {"entities" : qUnion([Q0, Q1, Q2, Q3, Q4, Q5, Q6, Q7, Q8, Q9, Q10]), "depth" : 3 * mm});
        }
    });
